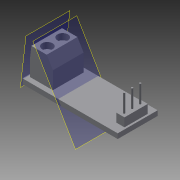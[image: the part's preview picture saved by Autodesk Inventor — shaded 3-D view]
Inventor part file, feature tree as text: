
AUTODESK INVENTOR PART (.ipt)
format: ipt  version: 2016 (Build 200138000, 138)  size: 177,664 bytes
history: native  units: in
note: dims shown in document units (in); Inventor stores cm internally (conversion verified against a paired STEP export)
features: extrude x9, sketch x9, plane x2, fillet x1
ambient origin geometry x8: Origin, YZ Plane, XZ Plane, XY Plane, X Axis, Y Axis, Z Axis, Center Point
bodies: Solid1 (feature_tree)
feature tree (21):
  extrude  "Extrusion1"  Depth=0.5118in
  extrude  "Extrusion2"  Depth=0.1102in TaperAngle=0.0deg
  extrude  "Extrusion3"  Depth=0.2992in
  extrude  "Extrusion4"  Depth=0.0236in
  extrude  "Extrusion5"  Depth=0.0236in
  plane  "Work Plane1"
  extrude  "Extrusion6"  Depth=0.0236in
  plane  "Work Plane2"
  extrude  "Extrusion7"  Depth=0.0512in
  extrude  "Extrusion8"  Depth=0.0787in
  extrude  "Extrusion9"  Depth=0.2283in TaperAngle=0.0deg
  fillet  "Fillet1"  Radius=0.2913in
  sketch  "Sketch1"  dims[d0=1.2205in d1=0.5118in]
  sketch  "Sketch2"  dims[d2=0.063in d3=0.0in d7=0.1102in d8=0.0in]
  sketch  "Sketch3"  dims[d9=0.1024in d10=0.2992in]
  sketch  "Sketch4"  dims[d12=0.1024in d13=0.0236in]
  sketch  "Sketch5"  dims[d14=0.0236in d15=0.0236in]
  sketch  "Sketch6"  dims[d16=0.0236in d17=0.0512in]
  sketch  "Sketch7"  dims[d18=0.0512in d19=0.0512in]
  sketch  "Sketch8"  dims[d20=0.0787in d21=0.0787in]
  sketch  "Sketch9"  dims[d22=0.0472in d23=0.2283in d24=0.0in d25=0.2913in d26=0.3937in d27=0.0354in d28=0.063in d29=0.2205in d30=0.0in d31=0.1969in d32=0.0in d33=0.0in d34=0.0787in d35=0.1339in d36=0.0in d37=0.0394in d38=0.0in d39=0.0787in d40=0.0in d41=0.1339in d42=0.1339in d43=0.0984in d44=0.1969in d45=0.1063in d46=0.1063in d47=0.0787in d48=0.0in d49=0.1575in d50=0.1969in d51=0.0787in d52=0.1575in d53=0.0551in d54=0.0in d55=0.0079in]
